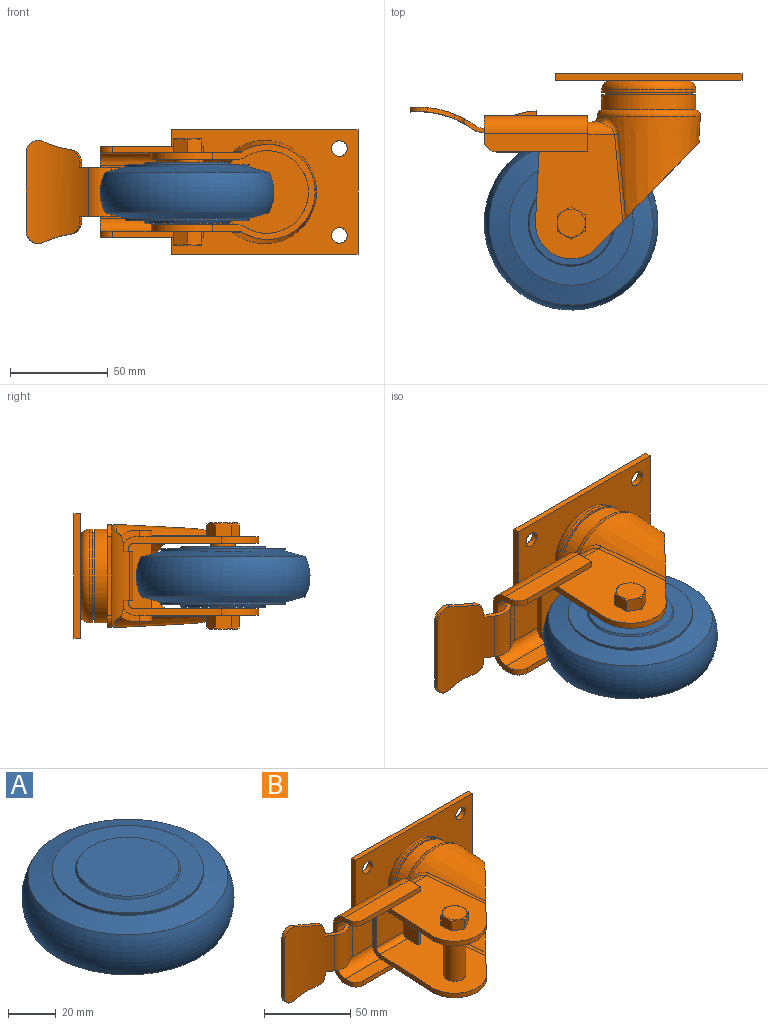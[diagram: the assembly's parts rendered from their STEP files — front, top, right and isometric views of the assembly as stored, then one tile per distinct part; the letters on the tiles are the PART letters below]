
ASSEMBLY  parts=2 mates=1
PART A: 15 faces, bbox 96.2x96.2x31.3 mm
  f0: cone r=21.43mm half-angle=30deg, axis (0,0,1), area 170.3mm2, adj f13,f14
  f1: cone r=20.67mm half-angle=10deg, axis (0,0,-1), area 25.1mm2, adj f12,f13
  f2: cylinder r=31.75mm len=63.5mm, axis (0,0,-1), area 253.4mm2, adj f3,f12
  f3: cone r=31.75mm half-angle=75deg, axis (0,0,1), area 2434.1mm2, adj f2,f4
  f4: torus R=22.32mm, axis (0,0,-1), area 5866.4mm2, adj f3,f5
  f5: cone r=41.91mm half-angle=75deg, axis (0,0,-1), area 2434.1mm2, adj f4,f6
  f6: cylinder r=31.75mm len=63.5mm, axis (0,0,-1), area 253.4mm2, adj f5,f11
  f7: cone r=20.64mm half-angle=10deg, axis (0,0,1), area 25.1mm2, adj f10,f11
  f8: cone r=22.05mm half-angle=30deg, axis (0,0,-1), area 170.3mm2, adj f9,f10
  f9: plane 42.86x42.86mm, normal (0,0,1), area 1442.9mm2, adj f8
  f10: plane 44.11x44.11mm, normal (0,0,-1), area 185.7mm2, adj f7,f8
  f11: plane 63.5x63.5mm, normal (0,0,1), area 1828.9mm2, adj f6,f7
  f12: plane 63.5x63.5mm, normal (0,0,-1), area 1828.9mm2, adj f1,f2
  f13: plane 44.11x44.11mm, normal (0,0,1), area 185.7mm2, adj f0,f1
  f14: plane 42.86x42.86mm, normal (0,0,-1), area 1442.9mm2, adj f0
PART B: 120 faces, bbox 181.6x106.4x75.4 mm
  f0: cylinder r=6.35mm len=9.13mm, axis (0,1,0), area 29.5mm2, adj f102,f103,f114,f117
  f1: cylinder r=6.35mm len=33.66mm, axis (0,0,-1), area 1342.8mm2, adj f31,f32
  f2: cone r=23.37mm half-angle=3deg, axis (0,1,0), area 3404.1mm2, adj f44,f48,f49,f50,f51,f52
  f3: cylinder r=18.26mm len=31.36mm, axis (0,0,-1), area 140.5mm2, adj f30,f32,f43,f44
  f4: cylinder r=18.26mm len=31.36mm, axis (0,0,-1), area 140.5mm2, adj f29,f31,f43,f44
  f5: torus R=23.2mm, axis (0,-1,0), area 813.2mm2, adj f6,f20,f39,f40,f41
  f6: cone r=26.54mm half-angle=3deg, axis (0,1,0), area 3376mm2, adj f5,f36,f37,f38,f42,f44
  f7: cylinder r=24mm len=48.01mm, axis (0,1,0), area 1153mm2, adj f20,f28
  f8: cylinder r=22.23mm len=44.45mm, axis (0,1,0), area 159.6mm2, adj f27,f28
  f9: cylinder r=24mm len=48.01mm, axis (0,1,0), area 229.8mm2, adj f10,f27
  f10: torus R=19.24mm, axis (0,1,0), area 1046.9mm2, adj f9,f21
  f11: cylinder r=3.97mm len=7.94mm, axis (0,1,0), area 79.2mm2, adj f21,f26
  f12: cylinder r=3.97mm len=7.94mm, axis (0,1,0), area 79.2mm2, adj f21,f26
  f13: cylinder r=3.97mm len=7.94mm, axis (0,1,0), area 79.2mm2, adj f21,f26
  f14: cylinder r=3.97mm len=7.94mm, axis (0,1,0), area 79.2mm2, adj f21,f26
  f15: plane 22.89x6.84mm, normal (0,0,1), area 50.4mm2, adj f97,f101,f102,f103,f104,f105,f106,f113
  f16: plane 22.89x6.84mm, normal (0,0,-1), area 50.4mm2, adj f97,f101,f102,f103,f104,f105,f106,f112
  f17: cylinder r=3.17mm len=22.26mm, axis (-1,0,0), area 110.6mm2, adj f19,f31,f43,f83
  f18: cylinder r=3.17mm len=22.26mm, axis (1,0,0), area 110.6mm2, adj f19,f32,f43,f83
  f19: plane 27.31x22.09mm, normal (0,-1,0), area 603.3mm2, adj f17,f18,f43,f83
  f20: plane 48.01x48.01mm, normal (0,-1,0), area 119.5mm2, adj f5,f7
  f21: plane 95.25x63.5mm, normal (0,-1,0), area 4687.4mm2, adj f10,f11,f12,f13,f14,f22,f23,f24
  f22: plane 63.5x3.18mm, normal (-1,0,0), area 201.6mm2, adj f21,f23,f25,f26
  f23: plane 95.25x3.18mm, normal (0,0,-1), area 302.4mm2, adj f21,f22,f24,f26
  f24: plane 63.5x3.18mm, normal (1,0,0), area 201.6mm2, adj f21,f23,f25,f26
  f25: plane 95.25x3.18mm, normal (0,0,1), area 302.4mm2, adj f21,f22,f24,f26
  f26: plane 95.25x63.5mm, normal (0,1,0), area 5850.4mm2, adj f11,f12,f13,f14,f22,f23,f24,f25
  f27: plane 48.01x48.01mm, normal (0,-1,0), area 258.2mm2, adj f8,f9
  f28: plane 48.01x48.01mm, normal (0,1,0), area 258.2mm2, adj f7,f8
  f29: plane 63.51x44.62mm, normal (0,0,-1), area 2030.5mm2, adj f4,f35,f36,f43,f44,f69,f70,f71
  f30: plane 63.51x44.62mm, normal (0,0,1), area 2030.5mm2, adj f3,f34,f37,f43,f44,f56,f57,f58
  f31: plane 63.51x44.62mm, normal (0,0,1), area 2280.6mm2, adj f1,f4,f17,f43,f44,f52,f53,f82
  f32: plane 63.51x44.62mm, normal (0,0,-1), area 2280.6mm2, adj f1,f3,f18,f43,f44,f51,f54,f82
  f33: plane 27.31x4.93mm, normal (0,1,0), area 73.1mm2, adj f34,f35,f40,f86
  f34: cylinder r=6.35mm len=13.61mm, axis (1,0,0), area 92.5mm2, adj f30,f33,f41,f42,f86
  f35: cylinder r=6.35mm len=13.61mm, axis (-1,0,0), area 92.5mm2, adj f29,f33,f38,f39,f86
  f36: bspline ~44.45x5.78mm, area 82.2mm2, adj f6,f29,f38,f44
  f37: bspline ~44.45x5.78mm, area 82.2mm2, adj f6,f30,f42,f44
  f38: bspline ~9.36x9.12mm, area 39.4mm2, adj f6,f35,f36,f39
  f39: bspline ~4.12x3.4mm, area 10.9mm2, adj f5,f35,f38,f40
  f40: torus R=29.55mm, axis (0,-1,0), area 131.9mm2, adj f5,f33,f39,f41
  f41: bspline ~4.12x3.4mm, area 10.9mm2, adj f5,f34,f40,f42
  f42: bspline ~9.36x9.12mm, area 39.4mm2, adj f6,f34,f37,f41
  f43: plane 50.88x40.24mm, normal (-1,0.05,0), area 416mm2, adj f3,f4,f17,f18,f19,f29,f30,f31
  f44: plane 65.82x64.18mm, normal (0.72,-0.7,0), area 597.9mm2, adj f2,f3,f4,f6,f29,f30,f31,f32
  f45: torus R=29.55mm, axis (0,-1,0), area 244.4mm2, adj f46,f47,f48,f55
  f46: bspline ~6.78x6.46mm, area 15.4mm2, adj f45,f48,f50,f54
  f47: bspline ~6.78x6.46mm, area 15.4mm2, adj f45,f48,f49,f53
  f48: plane 46.41x46.41mm, normal (0,-1,0), area 1690.5mm2, adj f2,f45,f46,f47
  f49: bspline ~11.04x9.53mm, area 62.5mm2, adj f2,f47,f52,f53
  f50: bspline ~11.04x9.53mm, area 62.5mm2, adj f2,f46,f51,f54
  f51: bspline ~44.88x7.38mm, area 162.1mm2, adj f2,f32,f44,f50
  f52: bspline ~44.88x7.38mm, area 162.1mm2, adj f2,f31,f44,f49
  f53: cylinder r=3.17mm len=13.61mm, axis (-1,0,0), area 46.2mm2, adj f31,f47,f49,f55,f82
  f54: cylinder r=3.17mm len=13.61mm, axis (1,0,0), area 46.2mm2, adj f32,f46,f50,f55,f82
  f55: plane 27.31x4.93mm, normal (0,-1,0), area 73.1mm2, adj f45,f53,f54,f82
  f56: plane 7.92x7.82mm, normal (-0.5,-0.87,0), area 57.9mm2, adj f30,f57,f61,f63,f64
  f57: plane 7.92x7.82mm, normal (0.5,-0.87,0), area 57.9mm2, adj f30,f56,f58,f62,f63
  f58: plane 8.93x7.92mm, normal (1,0,0), area 57.9mm2, adj f30,f57,f59,f62,f67
  f59: plane 7.92x7.82mm, normal (0.5,0.87,0), area 57.9mm2, adj f30,f58,f60,f66,f67
  f60: plane 7.92x7.82mm, normal (-0.5,0.87,0), area 57.9mm2, adj f30,f59,f61,f65,f66
  f61: plane 8.93x7.92mm, normal (-1,0,0), area 57.9mm2, adj f30,f56,f60,f64,f65
  f62: cone r=7.14mm half-angle=60deg, axis (0,0,-1), area 5mm2, adj f57,f58,f68
  f63: cone r=7.14mm half-angle=60deg, axis (0,0,-1), area 5mm2, adj f56,f57,f68
  f64: cone r=7.14mm half-angle=60deg, axis (0,0,-1), area 5mm2, adj f56,f61,f68
  f65: cone r=7.14mm half-angle=60deg, axis (0,0,-1), area 5mm2, adj f60,f61,f68
  f66: cone r=7.14mm half-angle=60deg, axis (0,0,-1), area 5mm2, adj f59,f60,f68
  f67: cone r=7.14mm half-angle=60deg, axis (0,0,-1), area 5mm2, adj f58,f59,f68
  f68: plane 14.29x14.29mm, normal (0,0,1), area 160.3mm2, adj f62,f63,f64,f65,f66,f67
  f69: plane 7.92x7.82mm, normal (-0.5,-0.87,0), area 57.9mm2, adj f29,f70,f74,f76,f77
  f70: plane 7.92x7.82mm, normal (0.5,-0.87,0), area 57.9mm2, adj f29,f69,f71,f75,f76
  f71: plane 8.93x7.92mm, normal (1,0,0), area 57.9mm2, adj f29,f70,f72,f75,f80
  f72: plane 7.92x7.82mm, normal (0.5,0.87,0), area 57.9mm2, adj f29,f71,f73,f79,f80
  f73: plane 7.92x7.82mm, normal (-0.5,0.87,0), area 57.9mm2, adj f29,f72,f74,f78,f79
  f74: plane 8.93x7.92mm, normal (-1,0,0), area 57.9mm2, adj f29,f69,f73,f77,f78
  f75: cone r=7.14mm half-angle=60deg, axis (0,0,1), area 5mm2, adj f70,f71,f81
  f76: cone r=7.14mm half-angle=60deg, axis (0,0,1), area 5mm2, adj f69,f70,f81
  f77: cone r=7.14mm half-angle=60deg, axis (0,0,1), area 5mm2, adj f69,f74,f81
  f78: cone r=7.14mm half-angle=60deg, axis (0,0,1), area 5mm2, adj f73,f74,f81
  f79: cone r=7.14mm half-angle=60deg, axis (0,0,1), area 5mm2, adj f72,f73,f81
  f80: cone r=7.14mm half-angle=60deg, axis (0,0,1), area 5mm2, adj f71,f72,f81
  f81: plane 14.29x14.29mm, normal (0,0,-1), area 160.3mm2, adj f75,f76,f77,f78,f79,f80
  f82: plane 33.66x12.07mm, normal (1,0,0), area 401.7mm2, adj f31,f32,f53,f54,f55,f84
  f83: plane 33.66x12.07mm, normal (-1,0,0), area 401.7mm2, adj f17,f18,f19,f31,f32,f84
  f84: plane 33.66x2.2mm, normal (0,-1,0), area 74.1mm2, adj f31,f32,f82,f83
  f85: plane 46.65x3.18mm, normal (0,-1,0), area 148.1mm2, adj f29,f86,f89,f92,f100
  f86: plane 46.36x18.42mm, normal (1,0,0), area 227.3mm2, adj f29,f30,f33,f34,f35,f85,f88,f91
  f87: cylinder r=6.35mm len=6.35mm, axis (0,0,1), area 31.7mm2, adj f88,f90,f93,f99
  f88: plane 46.65x3.18mm, normal (0,-1,0), area 148.1mm2, adj f30,f86,f87,f93,f99
  f89: cylinder r=6.35mm len=6.35mm, axis (0,0,1), area 31.7mm2, adj f85,f90,f92,f100
  f90: plane 46.36x12.07mm, normal (-1,0,0), area 187mm2, adj f87,f89,f91,f92,f93,f94,f95,f96
  f91: plane 53x28.58mm, normal (0,1,0), area 1269.9mm2, adj f86,f90,f94,f95,f107,f109,f110,f111
  f92: plane 53x9.53mm, normal (0,0,-1), area 496.2mm2, adj f85,f86,f89,f90,f95
  f93: plane 53x9.53mm, normal (0,0,1), area 496.2mm2, adj f86,f87,f88,f90,f94
  f94: cylinder r=8.89mm len=53mm, axis (-1,0,0), area 740.2mm2, adj f86,f90,f91,f93
  f95: cylinder r=8.89mm len=53mm, axis (-1,0,0), area 740.2mm2, adj f86,f90,f91,f92
  f96: cylinder r=6.35mm len=28.87mm, axis (-1,0,0), area 286.3mm2, adj f43,f90,f97,f100
  f97: plane 28.87x27.31mm, normal (0,-1,0), area 661.7mm2, adj f15,f16,f43,f90,f96,f98,f105,f106
  f98: cylinder r=6.35mm len=28.87mm, axis (-1,0,0), area 286.3mm2, adj f43,f90,f97,f99
  f99: plane 28.54x8.89mm, normal (0,0,-1), area 243mm2, adj f43,f87,f88,f90,f98
  f100: plane 28.54x8.89mm, normal (0,0,1), area 243mm2, adj f43,f85,f89,f90,f96
  f101: cylinder r=7.94mm len=25.4mm, axis (0,0,-1), area 246.8mm2, adj f15,f16,f102,f105
  f102: cylinder r=50.8mm len=52.71mm, axis (0,0,-1), area 1530.8mm2, adj f0,f15,f16,f101,f112,f113,f114,f115
  f103: cylinder r=48.51mm len=52.71mm, axis (0,0,-1), area 1473.6mm2, adj f0,f15,f16,f104,f112,f113,f114,f115
  f104: cylinder r=10.22mm len=25.4mm, axis (0,0,-1), area 317.9mm2, adj f15,f16,f103,f106
  f105: cylinder r=42.11mm len=25.4mm, axis (0,0,-1), area 83mm2, adj f15,f16,f97,f101
  f106: cylinder r=39.82mm len=25.4mm, axis (0,0,-1), area 188mm2, adj f15,f16,f97,f104
  f107: cylinder r=39.82mm len=25.4mm, axis (0,0,-1), area 75.9mm2, adj f91,f108,f110,f111
  f108: plane 25.4x2.28mm, normal (1,0.05,0), area 58.1mm2, adj f107,f109,f110,f111
  f109: cylinder r=42.11mm len=25.4mm, axis (0,0,-1), area 325.1mm2, adj f91,f108,f110,f111
  f110: plane 12.61x2.54mm, normal (0,0,1), area 19.7mm2, adj f91,f107,f108,f109
  f111: plane 12.61x2.54mm, normal (0,0,-1), area 19.7mm2, adj f91,f107,f108,f109
  f112: plane 2.67x2mm, normal (0.88,-0.48,0), area 5.9mm2, adj f16,f102,f103,f118
  f113: plane 2.67x2mm, normal (0.88,-0.48,0), area 5.9mm2, adj f15,f102,f103,f119
  f114: plane 40.01x2.29mm, normal (-1,0,0), area 91.7mm2, adj f0,f102,f103,f115
  f115: cylinder r=6.35mm len=9.13mm, axis (0,1,0), area 29.5mm2, adj f102,f103,f114,f116
  f116: cylinder r=44mm len=14.11mm, axis (0,1,0), area 32.9mm2, adj f102,f103,f115,f118
  f117: cylinder r=44mm len=14.11mm, axis (0,1,0), area 32.9mm2, adj f0,f102,f103,f119
  f118: bspline ~6.47x6.3mm, area 21.2mm2, adj f102,f103,f112,f116
  f119: bspline ~6.47x6.3mm, area 21.2mm2, adj f102,f103,f113,f117
PLACE A t=(-23.15,12.62,0.05)mm
PLACE B t=(-23.15,12.62,0.36)mm fixed
MATE revolute A.f0 <-> B.f1  axis (0,0,1) through (-62.84,-63.58,15.6)mm
